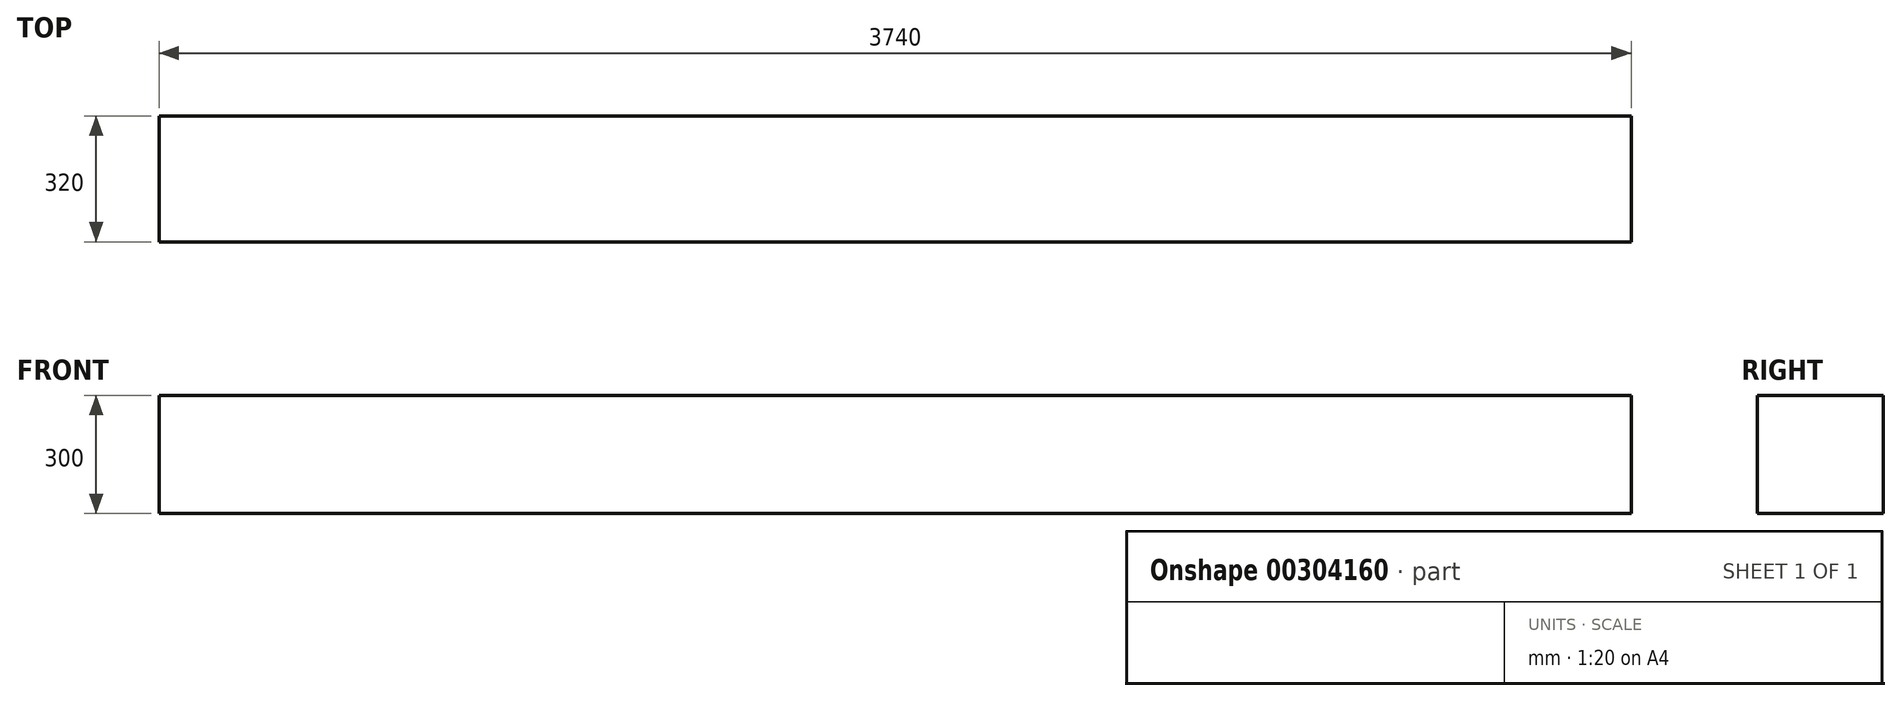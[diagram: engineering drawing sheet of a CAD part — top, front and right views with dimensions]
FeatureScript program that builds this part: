
annotation { "Feature Type Name" : "Feature", "Feature Type Description" : "" }
export const myFeature = defineFeature(function(context is Context, id is Id, definition is map)
    precondition{}
    {
        {
            var Q0;
            Q0=qCreatedBy(makeId("Top.planeOp"),FACE);
            var sketch = newSketch(context, id + "F0", { "sketchPlane" : qUnion([Q0])});
            skLineSegment(sketch, "E0.bottom", {"start": v(-1819.87, -35.85) * mm, "end": v(1920.13, -35.85) * mm});
            skLineSegment(sketch, "E0.top", {"start": v(-1819.87, -355.85) * mm, "end": v(1920.13, -355.85) * mm});
            skLineSegment(sketch, "E0.left", {"start": v(-1819.87, -35.85) * mm, "end": v(-1819.87, -355.85) * mm});
            skLineSegment(sketch, "E0.right", {"start": v(1920.13, -35.85) * mm, "end": v(1920.13, -355.85) * mm});
            skSolve(sketch);
        }
        {
            var Q0;
            Q0=makeQuery(id+"F0.imprint","IMPRINT",FACE,{"disambiguationData":[TD([[makeQuery(id+"F0.imprint","IMPRINT",EDGE,{"derivedFrom":sQuery(id+"F0.wireOp",EDGE,"E0.bottom")}),-1.0]])]});
            extrude(context, id + "F1", {"entities" : qUnion([Q0]), "depth" : 300 * mm});
        }
    });
